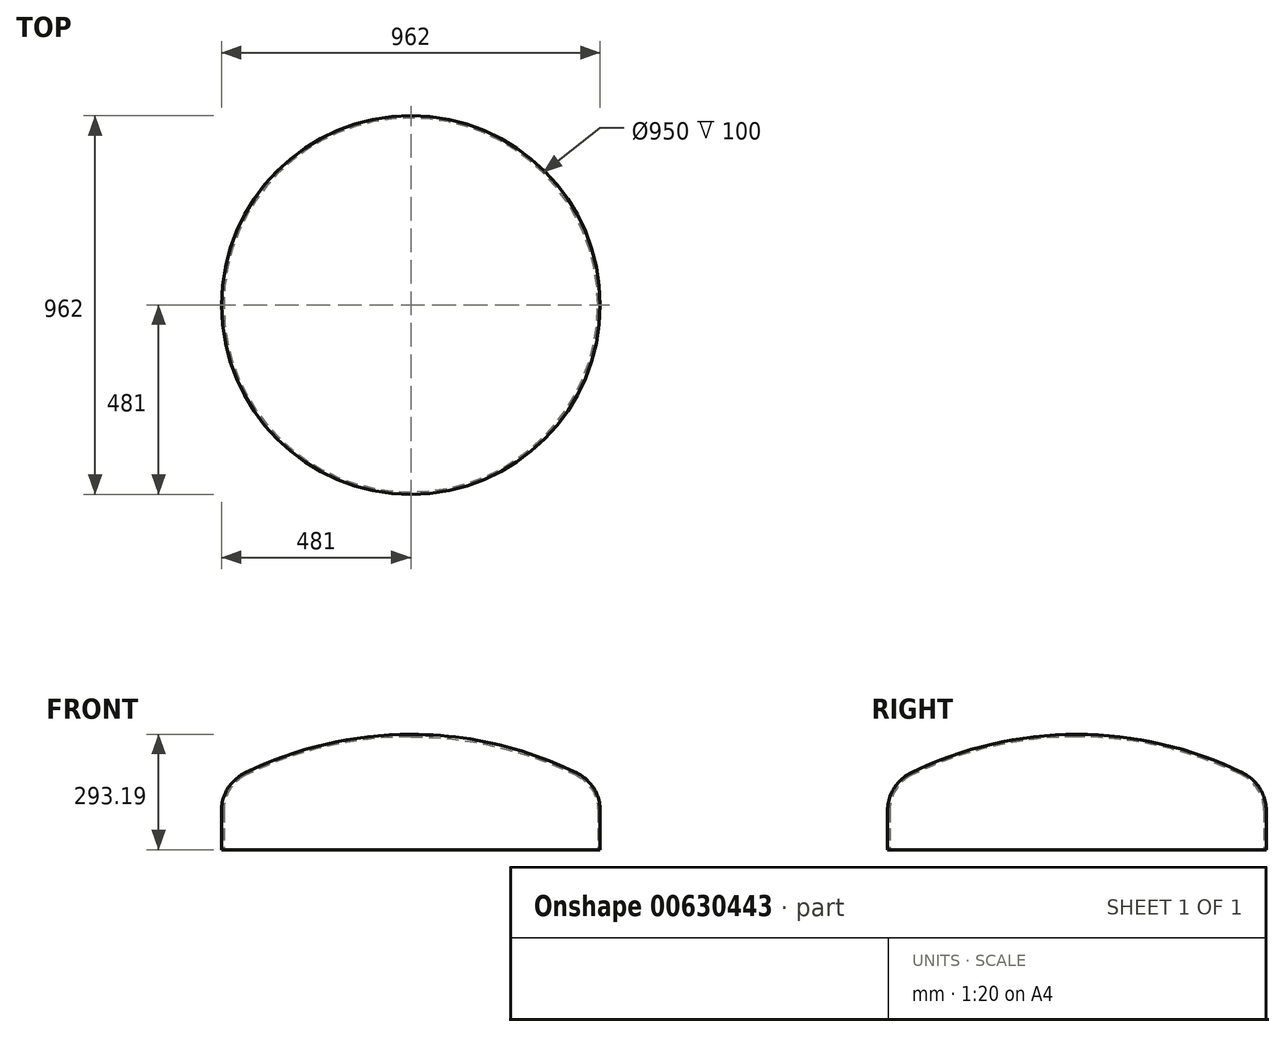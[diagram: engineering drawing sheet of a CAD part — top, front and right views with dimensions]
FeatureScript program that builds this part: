
annotation { "Feature Type Name" : "Feature", "Feature Type Description" : "" }
export const myFeature = defineFeature(function(context is Context, id is Id, definition is map)
    precondition{}
    {
        {
            var Q0;
            Q0=qCreatedBy(makeId("Front.planeOp"),FACE);
            var sketch = newSketch(context, id + "F0", { "sketchPlane" : qUnion([Q0])});
            skLineSegment(sketch, "E0", {"start": v(0, -386.08) * mm, "end": v(0, 1522.4) * mm, "construction": true});
            skArc(sketch, "E1", {"start": v(475, 100) * mm, "mid": v(459.89, 152.86) * mm, "end": v(419.12, 189.74) * mm});
            skLineSegment(sketch, "E2", {"start": v(475, 100) * mm, "end": v(475, 0) * mm});
            skArc(sketch, "E3", {"start": v(419.12, 189.74) * mm, "mid": v(215.15, 262.5) * mm, "end": v(0, 287.2) * mm});
            skLineSegment(sketch, "E4.0", {"start": v(481, 100) * mm, "end": v(481, 0) * mm});
            skArc(sketch, "E4.1", {"start": v(481, 100) * mm, "mid": v(464.98, 156.03) * mm, "end": v(421.76, 195.13) * mm});
            skArc(sketch, "E4.2", {"start": v(421.76, 195.13) * mm, "mid": v(216.5, 268.35) * mm, "end": v(0, 293.2) * mm});
            skLineSegment(sketch, "E5", {"start": v(0, 293.2) * mm, "end": v(0, 287.2) * mm});
            skLineSegment(sketch, "E6", {"start": v(475, 0) * mm, "end": v(481, 0) * mm});
            skSolve(sketch);
        }
        {
            var Q0;
            Q0=makeQuery(id+"F0.imprint","IMPRINT",FACE,{"disambiguationData":[TD([[makeQuery(id+"F0.imprint","IMPRINT",EDGE,{"derivedFrom":sQuery(id+"F0.wireOp",EDGE,"E1")}),-1.0]])]});
            var Q1;
            Q1=sQuery(id+"F0.wireOp",EDGE,"E0");
            revolve(context, id + "F1", {"entities" : qUnion([Q0]), "axis" : qUnion([Q1]), "revolveType" : RevolveType.FULL});
        }
    });
